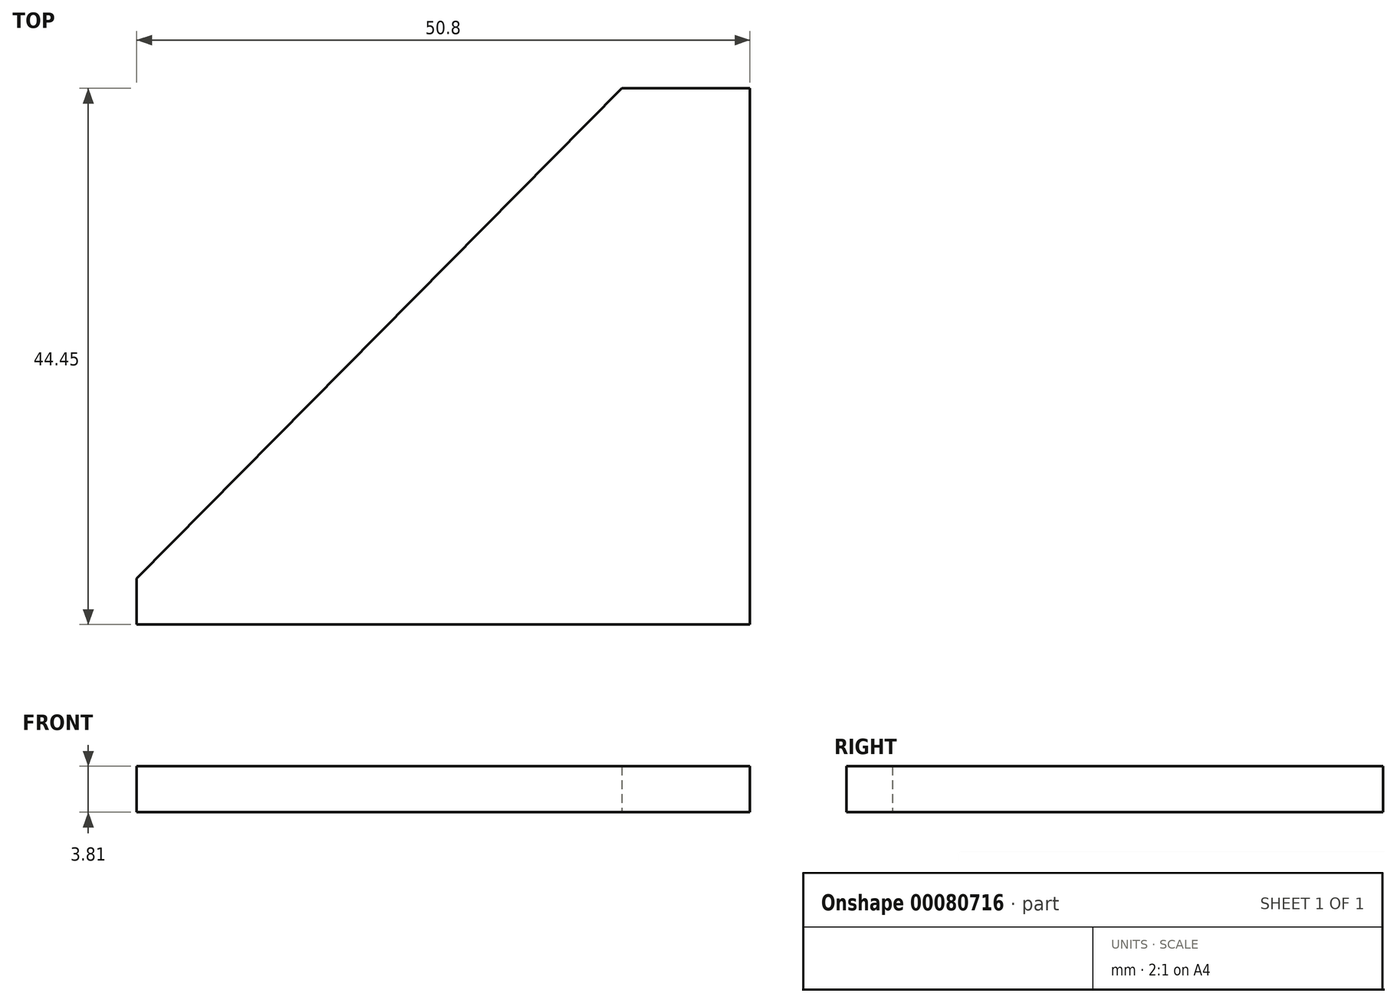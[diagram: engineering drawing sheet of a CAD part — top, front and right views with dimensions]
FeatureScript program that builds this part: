
annotation { "Feature Type Name" : "Feature", "Feature Type Description" : "" }
export const myFeature = defineFeature(function(context is Context, id is Id, definition is map)
    precondition{}
    {
        {
            var Q0;
            Q0=qCreatedBy(makeId("Top.planeOp"),FACE);
            var sketch = newSketch(context, id + "F0", { "sketchPlane" : qUnion([Q0])});
            skLineSegment(sketch, "E0.bottom", {"start": v(-61.87, 44.51) * mm, "end": v(-11.07, 44.51) * mm});
            skLineSegment(sketch, "E0.top", {"start": v(-61.87, 0.06) * mm, "end": v(-11.07, 0.06) * mm});
            skLineSegment(sketch, "E0.left", {"start": v(-61.87, 44.51) * mm, "end": v(-61.87, 0.06) * mm});
            skLineSegment(sketch, "E0.right", {"start": v(-11.07, 44.51) * mm, "end": v(-11.07, 0.06) * mm});
            skLineSegment(sketch, "E1", {"start": v(-61.87, 3.87) * mm, "end": v(-11.07, 3.87) * mm, "construction": true});
            skLineSegment(sketch, "E2", {"start": v(-61.87, 3.87) * mm, "end": v(-21.7, 44.51) * mm});
            skSolve(sketch);
        }
        {
            var Q0;
            {var subQ2=sQuery(id+"F0.wireOp",EDGE,"E0.top");Q0=makeQuery(id+"F0.imprint","IMPRINT",FACE,{"disambiguationData":[TD([[makeQuery(id+"F0.imprint","IMPRINT",EDGE,{"derivedFrom":subQ2}),1.0]])]});}
            extrude(context, id + "F1", {"entities" : qUnion([Q0]), "depth" : 3.8 * mm});
        }
    });
